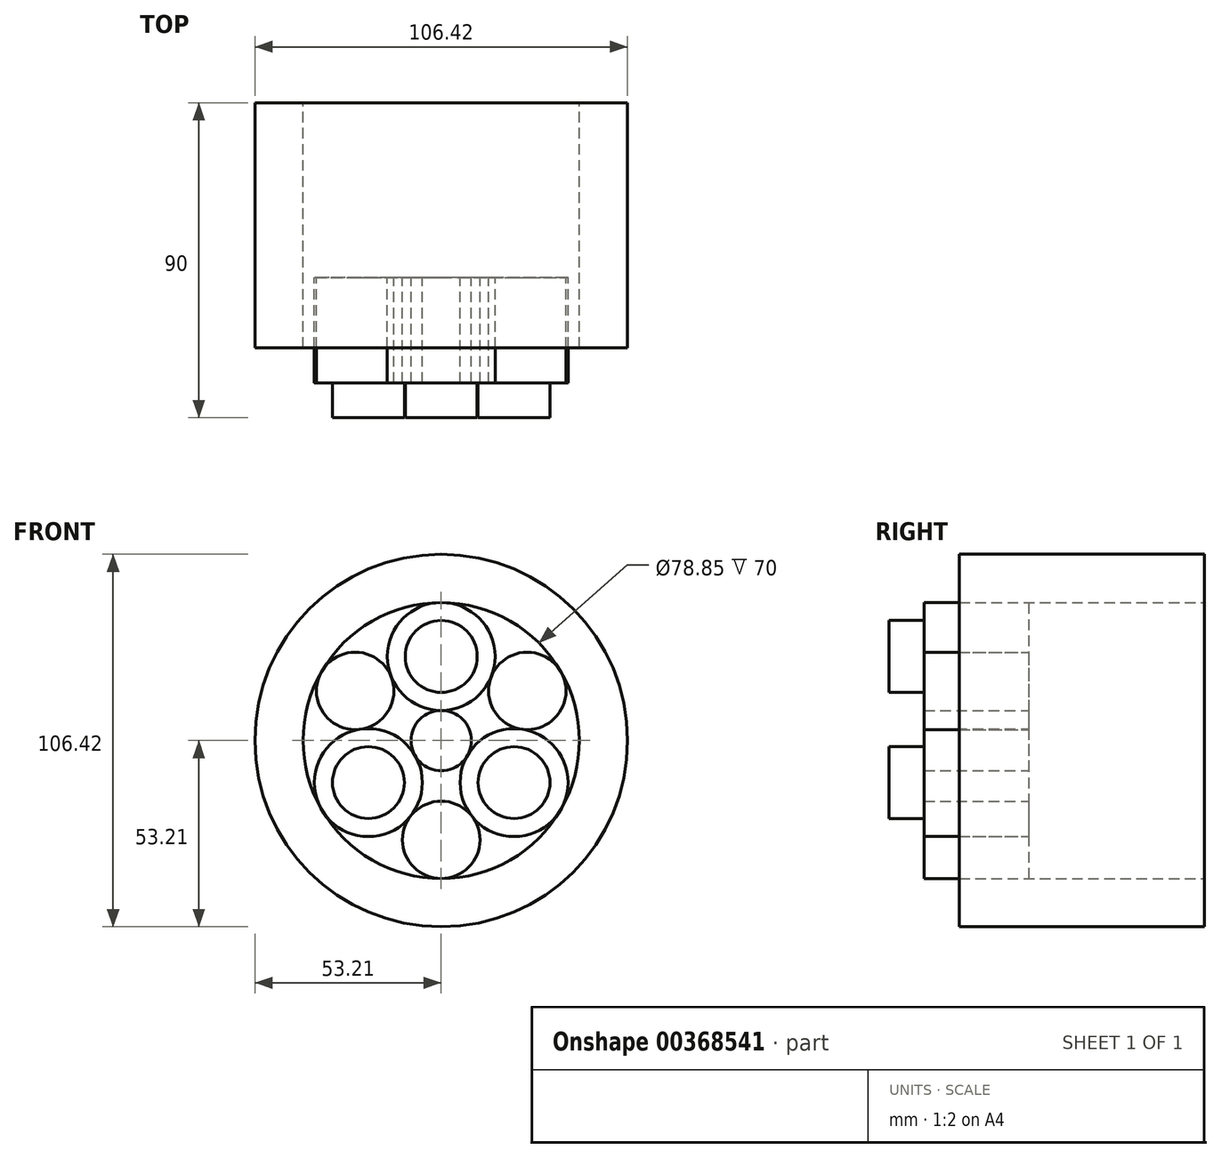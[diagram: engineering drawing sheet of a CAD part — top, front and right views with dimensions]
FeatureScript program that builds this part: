
annotation { "Feature Type Name" : "Feature", "Feature Type Description" : "" }
export const myFeature = defineFeature(function(context is Context, id is Id, definition is map)
    precondition{}
    {
        {
            var Q0;
            Q0=qCreatedBy(makeId("Front.planeOp"),FACE);
            var sketch = newSketch(context, id + "F0", { "sketchPlane" : qUnion([Q0])});
            skCircle(sketch, "E0", {"center": v(0, 0) * mm, "radius": 8.61 * mm});
            skCircle(sketch, "E1", {"center": v(0, 24.02) * mm, "radius": 15.4 * mm});
            skCircle(sketch, "E2.1.0", {"center": v(-20.8, -12) * mm, "radius": 15.4 * mm});
            skCircle(sketch, "E2.2.0", {"center": v(20.8, -12) * mm, "radius": 15.4 * mm});
            skCircle(sketch, "E3", {"center": v(0, 0) * mm, "radius": 39.42 * mm});
            skCircle(sketch, "E4", {"center": v(0, 0) * mm, "radius": 53.2 * mm});
            skCircle(sketch, "E5", {"center": v(-24.57, 14.18) * mm, "radius": 11.06 * mm});
            skPoint(sketch, "E5.first.point", {"position": v(-34.14, 19.71) * mm});
            skPoint(sketch, "E5.second.point", {"position": v(-23, 3.24) * mm});
            skPoint(sketch, "E5.third.point", {"position": v(-14.3, 18.3) * mm});
            skCircle(sketch, "E6.1.0", {"center": v(0, -28.37) * mm, "radius": 11.06 * mm});
            skCircle(sketch, "E6.2.0", {"center": v(24.57, 14.18) * mm, "radius": 11.06 * mm});
            skCircle(sketch, "E7", {"center": v(0, 24.02) * mm, "radius": 10.27 * mm});
            skCircle(sketch, "E8.1.0", {"center": v(-20.8, -12) * mm, "radius": 10.27 * mm});
            skCircle(sketch, "E8.2.0", {"center": v(20.8, -12) * mm, "radius": 10.27 * mm});
            skSolve(sketch);
        }
        {
            var Q0;
            Q0=makeQuery(id+"F0.imprint","IMPRINT",FACE,{"disambiguationData":[TD([[makeQuery(id+"F0.imprint","IMPRINT",EDGE,{"derivedFrom":sQuery(id+"F0.wireOp",EDGE,"E7")}),1.0]])]});
            extrude(context, id + "F1", {"entities" : qUnion([Q0]), "depth" : 40 * mm});
        }
        {
            var Q0;
            Q0=makeQuery(id+"F0.imprint","IMPRINT",FACE,{"disambiguationData":[TD([[makeQuery(id+"F0.imprint","IMPRINT",EDGE,{"derivedFrom":sQuery(id+"F0.wireOp",EDGE,"E7")}),-1.0]])]});
            extrude(context, id + "F2", {"entities" : qUnion([Q0]), "operationType" : NewBodyOperationType.ADD, "depth" : 30 * mm});
        }
        {
            var Q0;
            Q0=makeQuery(id+"F0.imprint","IMPRINT",FACE,{"disambiguationData":[TD([[makeQuery(id+"F0.imprint","IMPRINT",EDGE,{"derivedFrom":sQuery(id+"F0.wireOp",EDGE,"E8.1.0")}),-1.0]])]});
            extrude(context, id + "F3", {"entities" : qUnion([Q0]), "depth" : 30 * mm});
        }
        {
            var Q0;
            Q0=makeQuery(id+"F0.imprint","IMPRINT",FACE,{"disambiguationData":[TD([[makeQuery(id+"F0.imprint","IMPRINT",EDGE,{"derivedFrom":sQuery(id+"F0.wireOp",EDGE,"E8.1.0")}),1.0]])]});
            extrude(context, id + "F4", {"entities" : qUnion([Q0]), "operationType" : NewBodyOperationType.ADD, "depth" : 40 * mm});
        }
        {
            var Q0;
            Q0=makeQuery(id+"F0.imprint","IMPRINT",FACE,{"disambiguationData":[TD([[makeQuery(id+"F0.imprint","IMPRINT",EDGE,{"derivedFrom":sQuery(id+"F0.wireOp",EDGE,"E8.2.0")}),-1.0]])]});
            extrude(context, id + "F5", {"entities" : qUnion([Q0]), "depth" : 30 * mm});
        }
        {
            var Q0;
            Q0=makeQuery(id+"F0.imprint","IMPRINT",FACE,{"disambiguationData":[TD([[makeQuery(id+"F0.imprint","IMPRINT",EDGE,{"derivedFrom":sQuery(id+"F0.wireOp",EDGE,"E8.2.0")}),1.0]])]});
            extrude(context, id + "F6", {"entities" : qUnion([Q0]), "operationType" : NewBodyOperationType.ADD, "depth" : 40 * mm});
        }
        {
            var Q0;
            {var subQ0=sQuery(id+"F0.wireOp",EDGE,"E5");var subQ1=makeQuery(id+"F0.imprint","INTERSECT",VERTEX,{"derivedFrom":[sQuery(id+"F0.wireOp",EDGE,"E1"),subQ0]});Q0=makeQuery(id+"F0.imprint","IMPRINT",FACE,{"disambiguationData":[TD([[makeQuery(id+"F0.imprint","IMPRINT",EDGE,{"disambiguationData":[TD([[subQ1,-1.0]])],"derivedFrom":subQ0}),1.0]])]});}
            extrude(context, id + "F7", {"entities" : qUnion([Q0]), "depth" : 30 * mm});
        }
        {
            var Q0;
            {var subQ0=sQuery(id+"F0.wireOp",EDGE,"E6.2.0");var subQ1=makeQuery(id+"F0.imprint","INTERSECT",VERTEX,{"derivedFrom":[sQuery(id+"F0.wireOp",EDGE,"E2.2.0"),subQ0]});Q0=makeQuery(id+"F0.imprint","IMPRINT",FACE,{"disambiguationData":[TD([[makeQuery(id+"F0.imprint","IMPRINT",EDGE,{"disambiguationData":[TD([[subQ1,-1.0]])],"derivedFrom":subQ0}),1.0]])]});}
            extrude(context, id + "F8", {"entities" : qUnion([Q0]), "depth" : 30 * mm});
        }
        {
            var Q0;
            {var subQ0=sQuery(id+"F0.wireOp",EDGE,"E6.1.0");var subQ1=makeQuery(id+"F0.imprint","INTERSECT",VERTEX,{"derivedFrom":[sQuery(id+"F0.wireOp",EDGE,"E2.1.0"),subQ0]});Q0=makeQuery(id+"F0.imprint","IMPRINT",FACE,{"disambiguationData":[TD([[makeQuery(id+"F0.imprint","IMPRINT",EDGE,{"disambiguationData":[TD([[subQ1,-1.0]])],"derivedFrom":subQ0}),1.0]])]});}
            extrude(context, id + "F9", {"entities" : qUnion([Q0]), "depth" : 30 * mm});
        }
        {
            var Q0;
            {var subQ0=sQuery(id+"F0.wireOp",EDGE,"E0");var subQ1=makeQuery(id+"F0.imprint","INTERSECT",VERTEX,{"derivedFrom":[subQ0,sQuery(id+"F0.wireOp",EDGE,"E2.1.0")]});Q0=makeQuery(id+"F0.imprint","IMPRINT",FACE,{"disambiguationData":[TD([[makeQuery(id+"F0.imprint","IMPRINT",EDGE,{"disambiguationData":[TD([[subQ1,1.0]])],"derivedFrom":subQ0}),1.0]])]});}
            extrude(context, id + "F10", {"entities" : qUnion([Q0]), "depth" : 30 * mm});
        }
        {
            var Q0;
            Q0=makeQuery(id+"F0.imprint","IMPRINT",FACE,{"disambiguationData":[TD([[makeQuery(id+"F0.imprint","IMPRINT",EDGE,{"derivedFrom":sQuery(id+"F0.wireOp",EDGE,"E4")}),1.0]])]});
            extrude(context, id + "F11", {"entities" : qUnion([Q0]), "depth" : 20 * mm, "hasSecondDirection" : true, "secondDirectionOppositeDirection" : true, "secondDirectionDepth" : 50 * mm});
        }
    });
